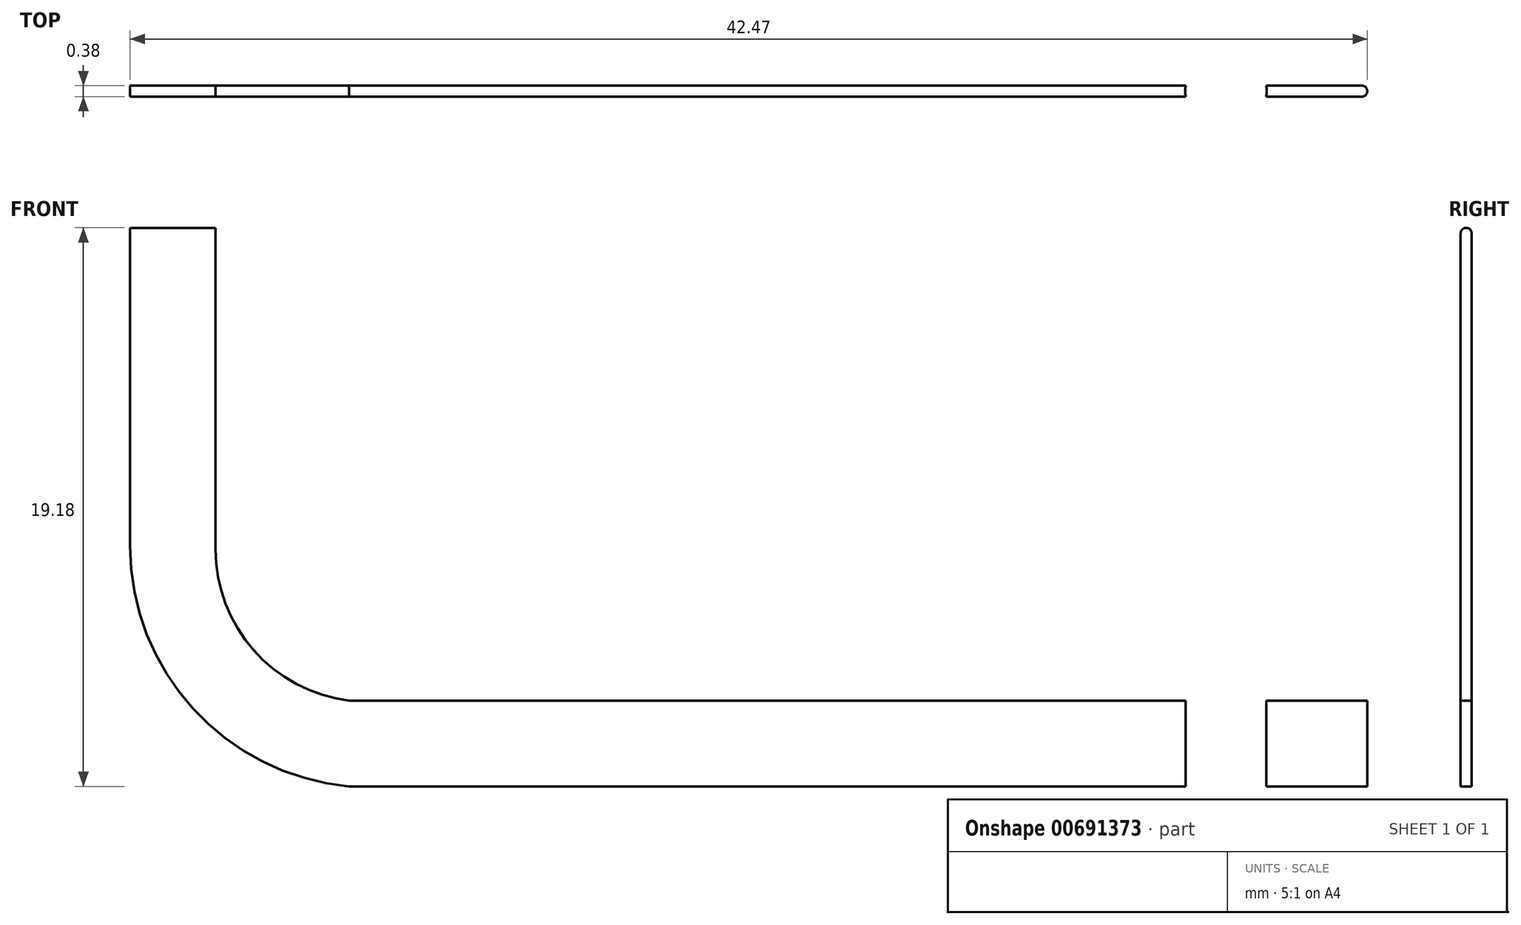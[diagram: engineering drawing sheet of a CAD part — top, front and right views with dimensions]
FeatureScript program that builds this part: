
annotation { "Feature Type Name" : "Feature", "Feature Type Description" : "" }
export const myFeature = defineFeature(function(context is Context, id is Id, definition is map)
    precondition{}
    {
        {
            assignVariable(context, id + "F0", {"name" : "width", "anyValue" : .382});
        }
        {
            var Q0;
            Q0=qCreatedBy(makeId("Front.planeOp"),FACE);
            var sketch = newSketch(context, id + "F1", { "sketchPlane" : qUnion([Q0])});
            skLineSegment(sketch, "E0.bottom", {"start": v(0, 0) * mm, "end": v(34.96, 0) * mm});
            skLineSegment(sketch, "E0.top", {"start": v(0, 2.95) * mm, "end": v(34.96, 2.95) * mm});
            skLineSegment(sketch, "E0.right", {"start": v(34.96, 0) * mm, "end": v(34.96, 2.95) * mm});
            skLineSegment(sketch, "E1.top", {"start": v(-7.51, 19.18) * mm, "end": v(-4.58, 19.18) * mm});
            skLineSegment(sketch, "E1.left", {"start": v(-7.51, 8.26) * mm, "end": v(-7.51, 19.18) * mm});
            skLineSegment(sketch, "E1.right", {"start": v(-4.58, 8.14) * mm, "end": v(-4.58, 19.18) * mm});
            skArc(sketch, "E2", {"start": v(-4.58, 8.14) * mm, "mid": v(-3.27, 4.68) * mm, "end": v(0, 2.95) * mm});
            skArc(sketch, "E3", {"start": v(-7.51, 8.26) * mm, "mid": v(-5.35, 2.68) * mm, "end": v(0, 0) * mm});
            skSolve(sketch);
        }
        {
            var Q0;
            Q0=makeQuery(id+"F1.imprint","IMPRINT",FACE,{"disambiguationData":[TD([[makeQuery(id+"F1.imprint","IMPRINT",EDGE,{"derivedFrom":sQuery(id+"F1.wireOp",EDGE,"E0.bottom")}),1.0]])]});
            extrude(context, id + "F2", {"entities" : qUnion([Q0]), "endBound" : BoundingType.SYMMETRIC, "depth" : (getVariable(context, 'width')) * mm, "offsetDistance" : 25.4 * mm});
        }
        {
            var Q0;
            Q0=makeQuery(id+"F2.opExtrude","CAP_EDGE",EDGE,{"disambiguationData":[OSD([sQuery(id+"F1.wireOp",EDGE,"E0.right")])],"isStart":false});
            var Q1;
            Q1=makeQuery(id+"F2.opExtrude","CAP_EDGE",EDGE,{"disambiguationData":[OSD([sQuery(id+"F1.wireOp",EDGE,"E0.right")])],"isStart":true});
            var Q2;
            Q2=makeQuery(id+"F2.opExtrude","CAP_EDGE",EDGE,{"disambiguationData":[OSD([sQuery(id+"F1.wireOp",EDGE,"E1.top")])],"isStart":false});
            var Q3;
            Q3=makeQuery(id+"F2.opExtrude","CAP_EDGE",EDGE,{"disambiguationData":[OSD([sQuery(id+"F1.wireOp",EDGE,"E1.top")])],"isStart":true});
            fillet(context, id + "F3", {"entities" : qUnion([Q0, Q1, Q2, Q3]), "radius" : (getVariable(context, 'width') / 2) * mm, "tangentPropagation" : true, "allowEdgeOverflow" : false});
        }
        {
            var Q0;
            Q0=makeQuery(id+"F2.opExtrude","SWEPT_FACE",FACE,{"disambiguationData":[OSD([sQuery(id+"F1.wireOp",EDGE,"E0.top")])]});
            var sketch = newSketch(context, id + "F4", { "sketchPlane" : qUnion([Q0])});
            skLineSegment(sketch, "E4", {"start": v(30.1, 0) * mm, "end": v(34.96, 0) * mm, "construction": true});
            skCircle(sketch, "E5", {"center": v(30.1, 0) * mm, "radius": 1.4 * mm});
            skSolve(sketch);
        }
        {
            var Q0;
            Q0 = qSketchRegion(id + "F4", true);
            extrude(context, id + "F5", {"entities" : qUnion([Q0]), "operationType" : NewBodyOperationType.REMOVE, "oppositeDirection" : true, "depth" : 25.4 * mm, "offsetDistance" : 25.4 * mm});
        }
    });
